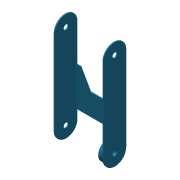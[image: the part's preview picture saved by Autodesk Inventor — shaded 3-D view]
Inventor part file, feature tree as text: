
AUTODESK INVENTOR PART (.ipt)
format: ipt  version: 2016 (Build 200138000, 138)  size: 157,184 bytes
history: native  units: in
note: dims shown in document units (in); Inventor stores cm internally (conversion verified against a paired STEP export)
features: extrude x5, sketch x5, plane x2, mirror x1, projected_geometry x1
ambient origin geometry x8: Origin, YZ Plane, XZ Plane, XY Plane, X Axis, Y Axis, Z Axis, Center Point
bodies: Solid1 (feature_tree)
feature tree (14):
  extrude  "Extrusion1"  Depth=8.6875in
  plane  "Work Plane2"
  mirror  "Mirror1"
  extrude  "Extrusion2"  Depth=4.875in
  extrude  "Extrusion3"  Depth=0.11in
  extrude  "Extrusion5"  Depth=0.11in TaperAngle=0.0deg
  extrude  "Extrusion4"  Depth=0.6in
  sketch  "Sketch1"  dims[d0=2.3125in d1=8.6875in]
  plane  "Work Plane1"
  sketch  "Sketch2"  dims[d2=0.11in d3=0.0in d4=4.875in d5=-2.4375in]
  sketch  "Sketch3"  dims[d6=3.9375in d7=0.11in]
  projected_geometry  "Projected Loop1"
  sketch  "Sketch4"  dims[d8=3.8125in d9=0.11in d10=0.0in]
  sketch  "Sketch5"  dims[d11=0.5in d12=0.5in d13=2.125in d14=1.75in d15=0.11in d16=0.0in d17=0.5in d18=0.5in d19=0.11in d20=0.0in d21=2.0in d22=0.6in d23=0.0in]
